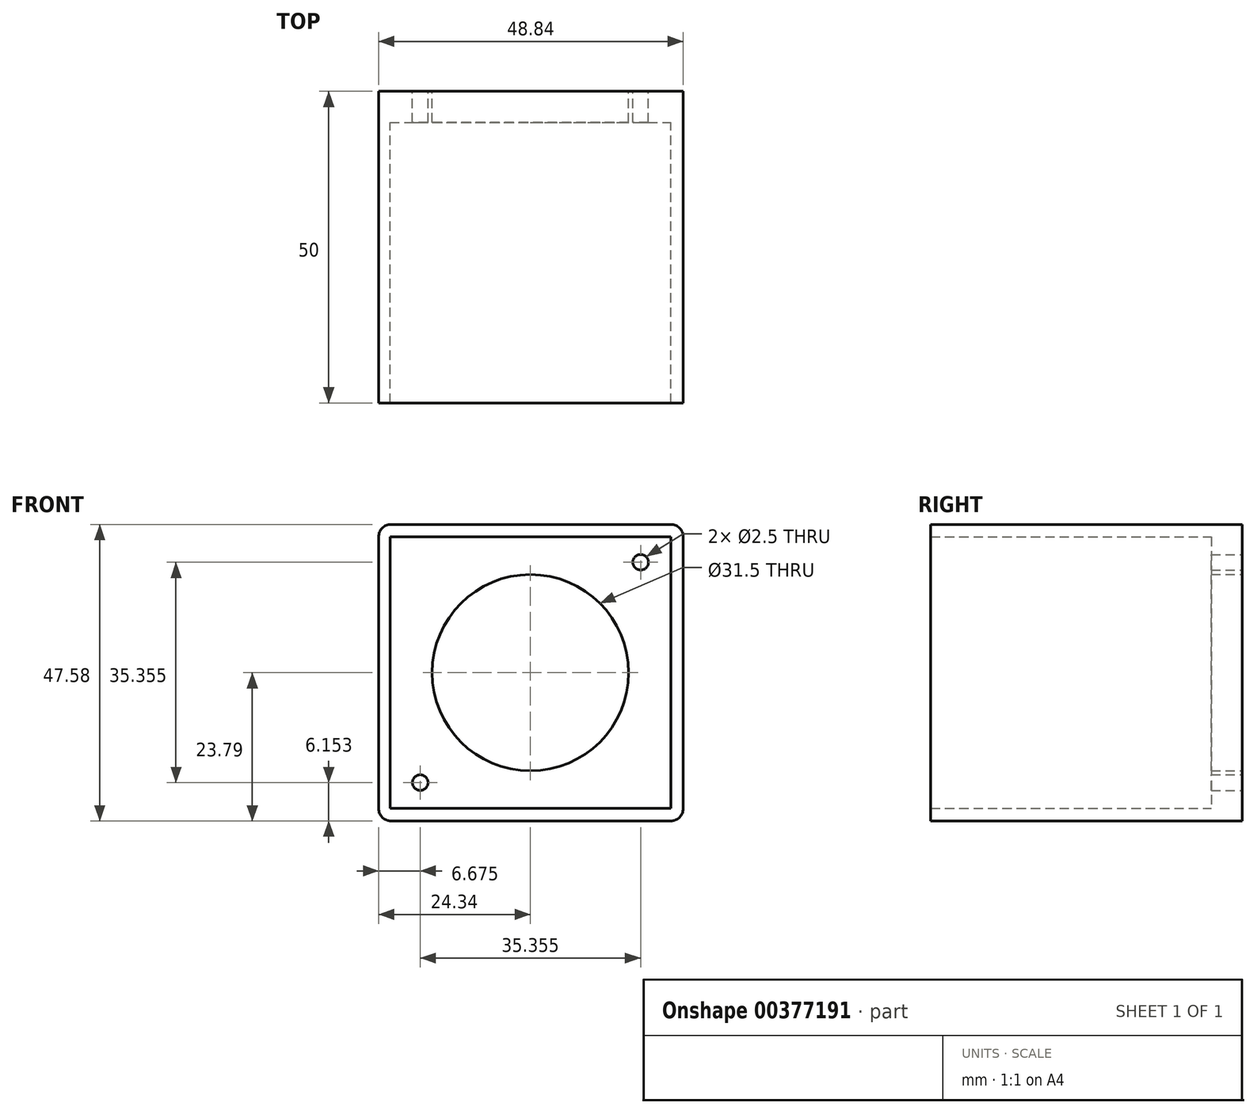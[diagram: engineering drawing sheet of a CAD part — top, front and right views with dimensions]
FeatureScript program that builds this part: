
annotation { "Feature Type Name" : "Feature", "Feature Type Description" : "" }
export const myFeature = defineFeature(function(context is Context, id is Id, definition is map)
    precondition{}
    {
        {
            var Q0;
            Q0=qCreatedBy(makeId("Front.planeOp"),FACE);
            var sketch = newSketch(context, id + "F0", { "sketchPlane" : qUnion([Q0])});
            skLineSegment(sketch, "E0", {"start": v(-21.02, -18.52) * mm, "end": v(-21.02, 7.29) * mm});
            skLineSegment(sketch, "E1", {"start": v(-21.02, 7.29) * mm, "end": v(-7.24, 21.08) * mm});
            skLineSegment(sketch, "E2", {"start": v(-7.24, 21.08) * mm, "end": v(18.57, 21.08) * mm});
            skLineSegment(sketch, "E3", {"start": v(21.05, 18.6) * mm, "end": v(21.05, -7.2) * mm});
            skLineSegment(sketch, "E4", {"start": v(21.05, -7.2) * mm, "end": v(7.26, -21) * mm});
            skLineSegment(sketch, "E5", {"start": v(7.26, -21) * mm, "end": v(-18.55, -21) * mm});
            skLineSegment(sketch, "E6", {"start": v(18.57, 21.08) * mm, "end": v(21.05, 18.6) * mm});
            skLineSegment(sketch, "E7", {"start": v(-21.02, -18.52) * mm, "end": v(-18.55, -21) * mm});
            skPoint(sketch, "E8.orphan", {"position": v(-21.02, -21) * mm});
            skPoint(sketch, "E9.orphan", {"position": v(21.05, 21.08) * mm});
            skLineSegment(sketch, "E10", {"start": v(0.01, 0.04) * mm, "end": v(17.7, 17.72) * mm, "construction": true});
            skLineSegment(sketch, "E11", {"start": v(0.01, 0.04) * mm, "end": v(-17.67, -17.64) * mm, "construction": true});
            skCircle(sketch, "E12", {"center": v(-17.67, -17.64) * mm, "radius": 1.25 * mm});
            skCircle(sketch, "E13", {"center": v(17.7, 17.72) * mm, "radius": 1.25 * mm});
            skCircle(sketch, "E14", {"center": v(0.01, 0.04) * mm, "radius": 13.85 * mm});
            skLineSegment(sketch, "E15.0", {"start": v(21.05, -7.2) * mm, "end": v(-7.24, 21.08) * mm, "construction": true});
            skLineSegment(sketch, "E16.0", {"start": v(7.26, -21) * mm, "end": v(-21.02, 7.29) * mm, "construction": true});
            skSolve(sketch);
        }
        {
            var Q0;
            Q0=qCreatedBy(makeId("Front.planeOp"),FACE);
            var sketch = newSketch(context, id + "F1", { "sketchPlane" : qUnion([Q0])});
            skCircle(sketch, "E17", {"center": v(0, 0) * mm, "radius": 15.75 * mm});
            skSolve(sketch);
        }
        {
            var Q0;
            Q0=qCreatedBy(makeId("Front.planeOp"),FACE);
            var sketch = newSketch(context, id + "F2", { "sketchPlane" : qUnion([Q0])});
            skLineSegment(sketch, "E18.bottom", {"start": v(22.5, -21.8) * mm, "end": v(-22.5, -21.8) * mm});
            skLineSegment(sketch, "E18.top", {"start": v(22.5, 21.8) * mm, "end": v(-22.5, 21.8) * mm});
            skLineSegment(sketch, "E18.left", {"start": v(22.5, -21.8) * mm, "end": v(22.5, 21.8) * mm});
            skLineSegment(sketch, "E18.right", {"start": v(-22.5, -21.8) * mm, "end": v(-22.5, 21.8) * mm});
            skPoint(sketch, "E18.middle", {"position": v(0, 0) * mm});
            skCircle(sketch, "E19.0", {"center": v(-17.67, -17.64) * mm, "radius": 1.25 * mm});
            skCircle(sketch, "E20.0", {"center": v(17.7, 17.72) * mm, "radius": 1.25 * mm});
            skCircle(sketch, "E21.0", {"center": v(0, 0) * mm, "radius": 15.75 * mm});
            skLineSegment(sketch, "E22.0", {"start": v(24.5, 23.8) * mm, "end": v(-24.34, 23.8) * mm});
            skLineSegment(sketch, "E22.1", {"start": v(24.5, -23.8) * mm, "end": v(24.5, 23.8) * mm});
            skLineSegment(sketch, "E22.2", {"start": v(24.5, -23.8) * mm, "end": v(-24.34, -23.8) * mm});
            skLineSegment(sketch, "E22.3", {"start": v(-24.34, -23.8) * mm, "end": v(-24.34, 23.8) * mm});
            skSolve(sketch);
        }
        {
            var Q0;
            Q0=makeQuery(id+"F2.imprint","IMPRINT",FACE,{"disambiguationData":[TD([[makeQuery(id+"F2.imprint","IMPRINT",EDGE,{"derivedFrom":sQuery(id+"F2.wireOp",EDGE,"E18.bottom")}),-1.0]])]});
            var Q1;
            Q1=makeQuery(id+"F2.imprint","IMPRINT",FACE,{"disambiguationData":[TD([[makeQuery(id+"F2.imprint","IMPRINT",EDGE,{"derivedFrom":sQuery(id+"F2.wireOp",EDGE,"E18.bottom")}),1.0]])]});
            extrude(context, id + "F3", {"entities" : qUnion([Q0, Q1]), "depth" : 5 * mm});
        }
        {
            var Q0;
            Q0=makeQuery(id+"F2.imprint","IMPRINT",FACE,{"disambiguationData":[TD([[makeQuery(id+"F2.imprint","IMPRINT",EDGE,{"derivedFrom":sQuery(id+"F2.wireOp",EDGE,"E18.bottom")}),1.0]])]});
            extrude(context, id + "F4", {"entities" : qUnion([Q0]), "operationType" : NewBodyOperationType.ADD, "depth" : 50 * mm});
        }
        {
            var Q0;
            {var subQ0=sQuery(id+"F2.wireOp",EDGE,"E22.3");var subQ1=sQuery(id+"F2.wireOp",EDGE,"E22.0");Q0=makeQuery(id+"F4.boolean.opBoolean","MERGE",EDGE,{"derivedFrom":[makeQuery(id+"F3.opExtrude","SWEPT_EDGE",EDGE,{"disambiguationData":[OSD([subQ1,subQ0])]}),makeQuery(id+"F4.opExtrude","SWEPT_EDGE",EDGE,{"disambiguationData":[OSD([subQ1,subQ0])]})]});}
            var Q1;
            {var subQ0=sQuery(id+"F2.wireOp",EDGE,"E22.1");var subQ1=sQuery(id+"F2.wireOp",EDGE,"E22.0");Q1=makeQuery(id+"F4.boolean.opBoolean","MERGE",EDGE,{"derivedFrom":[makeQuery(id+"F3.opExtrude","SWEPT_EDGE",EDGE,{"disambiguationData":[OSD([subQ1,subQ0])]}),makeQuery(id+"F4.opExtrude","SWEPT_EDGE",EDGE,{"disambiguationData":[OSD([subQ1,subQ0])]})]});}
            var Q2;
            {var subQ0=sQuery(id+"F2.wireOp",EDGE,"E22.2");var subQ1=sQuery(id+"F2.wireOp",EDGE,"E22.1");Q2=makeQuery(id+"F4.boolean.opBoolean","MERGE",EDGE,{"derivedFrom":[makeQuery(id+"F3.opExtrude","SWEPT_EDGE",EDGE,{"disambiguationData":[OSD([subQ1,subQ0])]}),makeQuery(id+"F4.opExtrude","SWEPT_EDGE",EDGE,{"disambiguationData":[OSD([subQ1,subQ0])]})]});}
            var Q3;
            {var subQ0=sQuery(id+"F2.wireOp",EDGE,"E22.3");var subQ1=sQuery(id+"F2.wireOp",EDGE,"E22.2");Q3=makeQuery(id+"F4.boolean.opBoolean","MERGE",EDGE,{"derivedFrom":[makeQuery(id+"F3.opExtrude","SWEPT_EDGE",EDGE,{"disambiguationData":[OSD([subQ1,subQ0])]}),makeQuery(id+"F4.opExtrude","SWEPT_EDGE",EDGE,{"disambiguationData":[OSD([subQ1,subQ0])]})]});}
            fillet(context, id + "F5", {"entities" : qUnion([Q0, Q1, Q2, Q3]), "radius" : 2 * mm, "tangentPropagation" : true, "allowEdgeOverflow" : false});
        }
    });
